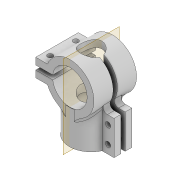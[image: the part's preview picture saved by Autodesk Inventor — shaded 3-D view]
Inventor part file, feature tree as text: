
AUTODESK INVENTOR PART (.ipt)
format: ipt  version: 2022 (Build 260153000, 153)  size: 334,336 bytes
history: native  units: mm
features: extrude x5, sketch x4, fillet x1
ambient origin geometry x8: Origin, YZ Plane, XZ Plane, XY Plane, X Axis, Y Axis, Z Axis, Center Point
bodies: Solid1 (feature_tree)
feature tree (10):
  sketch  "Sketch1"  dims[d0=35.0mm d1=8.0mm]
  extrude  "Extrusion1"  Depth=8.0mm
  extrude  "Extrusion4"  Depth=8.0mm
  extrude  "Extrusion5"  Depth=2.5mm
  fillet  "Fillet1"  Radius=20.0mm
  extrude  "Extrusion6"  Depth=10.0mm TaperAngle=0.0deg
  extrude  "Extrusion7"  Depth=10.0mm
  sketch  "Sketch4"  dims[d2=8.0mm d3=8.0mm]
  sketch  "Sketch5"  dims[d7=2.5mm d8=2.5mm d9=20.0mm]
  sketch  "Sketch6"  dims[d10=20.0mm d11=40.0mm d12=0.0mm d24=40.5mm d25=8.0mm d26=8.0mm d27=8.0mm d28=20.0mm d29=20.0mm d30=2.5mm d31=50.0mm d32=0.0mm d33=100.0mm d34=0.0mm d35=25.0mm d36=5.0mm d37=6.2mm d38=6.2mm d39=10.0mm d40=10.0mm d41=7.0mm d42=7.0mm d43=100.0mm d44=0.0mm d45=6.2mm d46=6.2mm d47=7.0mm d48=7.0mm d49=10.0mm d50=10.0mm d51=100.0mm d52=0.0mm]
